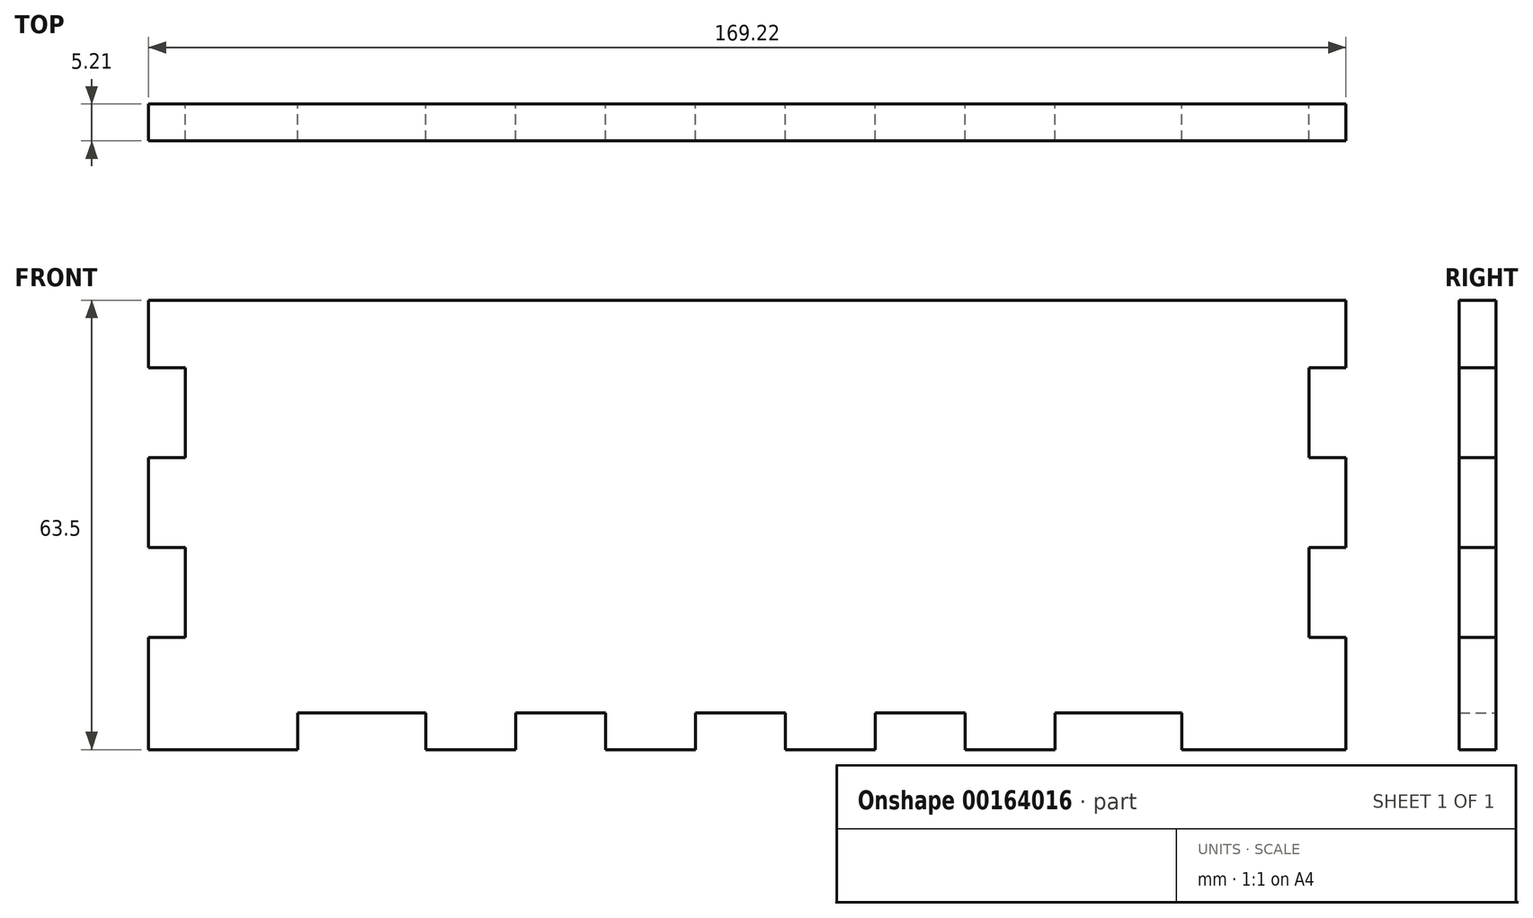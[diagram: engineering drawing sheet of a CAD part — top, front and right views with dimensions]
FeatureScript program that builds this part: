
annotation { "Feature Type Name" : "Feature", "Feature Type Description" : "" }
export const myFeature = defineFeature(function(context is Context, id is Id, definition is map)
    precondition{}
    {
        {
            var Q0;
            Q0=qCreatedBy(makeId("Front.planeOp"),FACE);
            var sketch = newSketch(context, id + "F0", { "sketchPlane" : qUnion([Q0])});
            skLineSegment(sketch, "E0.bottom", {"start": v(-84.61, -31.75) * mm, "end": v(84.61, -31.75) * mm});
            skLineSegment(sketch, "E0.top", {"start": v(-84.61, 31.75) * mm, "end": v(84.61, 31.75) * mm});
            skLineSegment(sketch, "E0.left", {"start": v(-84.61, -31.75) * mm, "end": v(-84.61, 31.75) * mm});
            skLineSegment(sketch, "E0.right", {"start": v(84.61, -31.75) * mm, "end": v(84.61, 31.75) * mm});
            skPoint(sketch, "E0.middle", {"position": v(0, 0) * mm});
            skSolve(sketch);
        }
        {
            var Q0;
            Q0=makeQuery(id+"F0.imprint","IMPRINT",FACE,{"disambiguationData":[TD([[makeQuery(id+"F0.imprint","IMPRINT",EDGE,{"derivedFrom":sQuery(id+"F0.wireOp",EDGE,"E0.bottom")}),1.0]])]});
            extrude(context, id + "F1", {"entities" : qUnion([Q0]), "depth" : 5.2 * mm});
        }
        {
            var Q0;
            Q0=makeQuery(id+"F1.opExtrude","CAP_FACE",FACE,{"disambiguationData":[OSD([sQuery(id+"F0.wireOp",EDGE,"E0.bottom"),sQuery(id+"F0.wireOp",EDGE,"E0.top"),sQuery(id+"F0.wireOp",EDGE,"E0.left"),sQuery(id+"F0.wireOp",EDGE,"E0.right")])],"isStart":true});
            var sketch = newSketch(context, id + "F2", { "sketchPlane" : qUnion([Q0])});
            skLineSegment(sketch, "E1", {"start": v(84.61, -31.75) * mm, "end": v(63.52, -31.75) * mm});
            skLineSegment(sketch, "E2", {"start": v(63.52, -31.75) * mm, "end": v(63.52, -26.54) * mm});
            skLineSegment(sketch, "E3", {"start": v(63.52, -26.54) * mm, "end": v(45.42, -26.54) * mm});
            skLineSegment(sketch, "E4", {"start": v(45.42, -26.54) * mm, "end": v(45.42, -31.75) * mm});
            skLineSegment(sketch, "E5", {"start": v(45.42, -31.75) * mm, "end": v(32.72, -31.75) * mm});
            skLineSegment(sketch, "E6", {"start": v(32.72, -31.75) * mm, "end": v(32.72, -26.54) * mm});
            skLineSegment(sketch, "E7", {"start": v(32.72, -26.54) * mm, "end": v(20.02, -26.54) * mm});
            skLineSegment(sketch, "E8", {"start": v(20.02, -26.54) * mm, "end": v(20.02, -31.75) * mm});
            skLineSegment(sketch, "E9", {"start": v(20.02, -31.75) * mm, "end": v(7.32, -31.75) * mm});
            skLineSegment(sketch, "E10", {"start": v(7.32, -31.75) * mm, "end": v(7.32, -26.54) * mm});
            skLineSegment(sketch, "E11", {"start": v(7.32, -26.54) * mm, "end": v(-5.38, -26.54) * mm});
            skLineSegment(sketch, "E12", {"start": v(-5.38, -26.54) * mm, "end": v(-5.38, -31.75) * mm});
            skLineSegment(sketch, "E13", {"start": v(-5.38, -31.75) * mm, "end": v(-18.08, -31.75) * mm});
            skLineSegment(sketch, "E14", {"start": v(-18.08, -31.75) * mm, "end": v(-18.08, -26.54) * mm});
            skLineSegment(sketch, "E15", {"start": v(-18.08, -26.54) * mm, "end": v(-30.78, -26.54) * mm});
            skLineSegment(sketch, "E16", {"start": v(-30.78, -26.54) * mm, "end": v(-30.78, -31.75) * mm});
            skLineSegment(sketch, "E17", {"start": v(-30.78, -31.75) * mm, "end": v(-43.48, -31.75) * mm});
            skLineSegment(sketch, "E18", {"start": v(-43.48, -31.75) * mm, "end": v(-43.48, -26.54) * mm});
            skLineSegment(sketch, "E19", {"start": v(-43.48, -26.54) * mm, "end": v(-61.43, -26.54) * mm});
            skLineSegment(sketch, "E20", {"start": v(-61.43, -26.54) * mm, "end": v(-61.42, -31.75) * mm});
            skLineSegment(sketch, "E21", {"start": v(-61.42, -31.75) * mm, "end": v(-84.61, -31.75) * mm});
            skLineSegment(sketch, "E22", {"start": v(-84.61, -31.75) * mm, "end": v(-84.61, -15.88) * mm});
            skLineSegment(sketch, "E23", {"start": v(-84.61, -15.88) * mm, "end": v(-79.4, -15.88) * mm});
            skLineSegment(sketch, "E24", {"start": v(-79.4, -15.88) * mm, "end": v(-79.4, -3.17) * mm});
            skLineSegment(sketch, "E25", {"start": v(-79.4, -3.18) * mm, "end": v(-84.61, -3.18) * mm});
            skLineSegment(sketch, "E26", {"start": v(-84.61, -3.17) * mm, "end": v(-84.61, 9.53) * mm});
            skLineSegment(sketch, "E27", {"start": v(-84.61, 9.52) * mm, "end": v(-79.4, 9.52) * mm});
            skLineSegment(sketch, "E28", {"start": v(-79.4, 9.53) * mm, "end": v(-79.4, 22.23) * mm});
            skLineSegment(sketch, "E29", {"start": v(-79.4, 22.22) * mm, "end": v(-84.61, 22.22) * mm});
            skLineSegment(sketch, "E30", {"start": v(-84.61, 22.23) * mm, "end": v(-84.61, 31.75) * mm});
            skLineSegment(sketch, "E31", {"start": v(84.61, -31.75) * mm, "end": v(84.61, -15.88) * mm});
            skLineSegment(sketch, "E32", {"start": v(84.61, -15.88) * mm, "end": v(79.4, -15.88) * mm});
            skLineSegment(sketch, "E33", {"start": v(79.4, -15.88) * mm, "end": v(79.4, -3.17) * mm});
            skLineSegment(sketch, "E34", {"start": v(79.4, -3.17) * mm, "end": v(84.61, -3.17) * mm});
            skLineSegment(sketch, "E35", {"start": v(84.61, -3.17) * mm, "end": v(84.61, 9.53) * mm});
            skLineSegment(sketch, "E36", {"start": v(84.61, 9.53) * mm, "end": v(79.4, 9.53) * mm});
            skLineSegment(sketch, "E37", {"start": v(79.4, 9.53) * mm, "end": v(79.4, 22.23) * mm});
            skLineSegment(sketch, "E38", {"start": v(79.4, 22.23) * mm, "end": v(84.61, 22.23) * mm});
            skLineSegment(sketch, "E39", {"start": v(84.61, 22.23) * mm, "end": v(84.61, 31.75) * mm});
            skSolve(sketch);
        }
        {
            var Q0;
            {var subQ0=sQuery(id+"F2.wireOp",EDGE,"E27");Q0=makeQuery(id+"F2.imprint","IMPRINT",FACE,{"disambiguationData":[TD([[makeQuery(id+"F2.imprint","IMPRINT",EDGE,{"derivedFrom":subQ0}),1.0]])]});}
            var Q1;
            {var subQ0=sQuery(id+"F2.wireOp",EDGE,"E23");Q1=makeQuery(id+"F2.imprint","IMPRINT",FACE,{"disambiguationData":[TD([[makeQuery(id+"F2.imprint","IMPRINT",EDGE,{"derivedFrom":subQ0}),1.0]])]});}
            var Q2;
            {var subQ0=sQuery(id+"F2.wireOp",EDGE,"E18");Q2=makeQuery(id+"F2.imprint","IMPRINT",FACE,{"disambiguationData":[TD([[makeQuery(id+"F2.imprint","IMPRINT",EDGE,{"derivedFrom":subQ0}),1.0]])]});}
            var Q3;
            {var subQ0=sQuery(id+"F2.wireOp",EDGE,"E14");Q3=makeQuery(id+"F2.imprint","IMPRINT",FACE,{"disambiguationData":[TD([[makeQuery(id+"F2.imprint","IMPRINT",EDGE,{"derivedFrom":subQ0}),1.0]])]});}
            var Q4;
            {var subQ0=sQuery(id+"F2.wireOp",EDGE,"E10");Q4=makeQuery(id+"F2.imprint","IMPRINT",FACE,{"disambiguationData":[TD([[makeQuery(id+"F2.imprint","IMPRINT",EDGE,{"derivedFrom":subQ0}),1.0]])]});}
            var Q5;
            {var subQ0=sQuery(id+"F2.wireOp",EDGE,"E6");Q5=makeQuery(id+"F2.imprint","IMPRINT",FACE,{"disambiguationData":[TD([[makeQuery(id+"F2.imprint","IMPRINT",EDGE,{"derivedFrom":subQ0}),1.0]])]});}
            var Q6;
            {var subQ0=sQuery(id+"F2.wireOp",EDGE,"E2");Q6=makeQuery(id+"F2.imprint","IMPRINT",FACE,{"disambiguationData":[TD([[makeQuery(id+"F2.imprint","IMPRINT",EDGE,{"derivedFrom":subQ0}),1.0]])]});}
            var Q7;
            {var subQ0=sQuery(id+"F2.wireOp",EDGE,"N13VfeZh-3YwB-qJvK-dNy5-TzPNthxaDaNM");Q7=makeQuery(id+"F2.imprint","IMPRINT",FACE,{"disambiguationData":[TD([[makeQuery(id+"F2.imprint","IMPRINT",EDGE,{"derivedFrom":subQ0}),-1.0]])]});}
            var Q8;
            {var subQ0=sQuery(id+"F2.wireOp",EDGE,"LjRXUlpK-2mOK-iaHC-AOVq-vGvUN4RJ73hQ");Q8=makeQuery(id+"F2.imprint","IMPRINT",FACE,{"disambiguationData":[TD([[makeQuery(id+"F2.imprint","IMPRINT",EDGE,{"derivedFrom":subQ0}),-1.0]])]});}
            var Q9;
            {var subQ0=sQuery(id+"F2.wireOp",EDGE,"TNSkxNZJ-b3q9-X5Cb-N7qb-4vqhPXFNXUM9");Q9=makeQuery(id+"F2.imprint","IMPRINT",FACE,{"disambiguationData":[TD([[makeQuery(id+"F2.imprint","IMPRINT",EDGE,{"derivedFrom":subQ0}),1.0]])]});}
            var Q10;
            {var subQ0=sQuery(id+"F2.wireOp",EDGE,"FjUMwnaR-dRpw-QTiK-HH9K-1Nnnlsrhm2u0");Q10=makeQuery(id+"F2.imprint","IMPRINT",FACE,{"disambiguationData":[TD([[makeQuery(id+"F2.imprint","IMPRINT",EDGE,{"derivedFrom":subQ0}),1.0]])]});}
            var Q11;
            {var subQ0=sQuery(id+"F2.wireOp",EDGE,"KaqQu8h5-b7EN-1yGX-7z54-1dn1vfCOI0mz");Q11=makeQuery(id+"F2.imprint","IMPRINT",FACE,{"disambiguationData":[TD([[makeQuery(id+"F2.imprint","IMPRINT",EDGE,{"derivedFrom":subQ0}),1.0]])]});}
            var Q12;
            {var subQ0=sQuery(id+"F2.wireOp",EDGE,"KmEVUEmv-pZ01-TFs3-ppWa-XZ57MDwfb18T");Q12=makeQuery(id+"F2.imprint","IMPRINT",FACE,{"disambiguationData":[TD([[makeQuery(id+"F2.imprint","IMPRINT",EDGE,{"derivedFrom":subQ0}),1.0]])]});}
            var Q13;
            {var subQ0=sQuery(id+"F2.wireOp",EDGE,"rpYDv9Ks-nJ08-Ut60-jELp-3Mz6rTRlvO3o");Q13=makeQuery(id+"F2.imprint","IMPRINT",FACE,{"disambiguationData":[TD([[makeQuery(id+"F2.imprint","IMPRINT",EDGE,{"derivedFrom":subQ0}),1.0]])]});}
            var Q14;
            {var subQ0=sQuery(id+"F2.wireOp",EDGE,"E36");Q14=makeQuery(id+"F2.imprint","IMPRINT",FACE,{"disambiguationData":[TD([[makeQuery(id+"F2.imprint","IMPRINT",EDGE,{"derivedFrom":subQ0}),-1.0]])]});}
            var Q15;
            {var subQ0=sQuery(id+"F2.wireOp",EDGE,"E32");Q15=makeQuery(id+"F2.imprint","IMPRINT",FACE,{"disambiguationData":[TD([[makeQuery(id+"F2.imprint","IMPRINT",EDGE,{"derivedFrom":subQ0}),-1.0]])]});}
            extrude(context, id + "F3", {"entities" : qUnion([Q0, Q1, Q2, Q3, Q4, Q5, Q6, Q7, Q8, Q9, Q10, Q11, Q12, Q13, Q14, Q15]), "operationType" : NewBodyOperationType.REMOVE, "endBound" : BoundingType.THROUGH_ALL, "oppositeDirection" : true, "depth" : 25.4 * mm});
        }
    });
